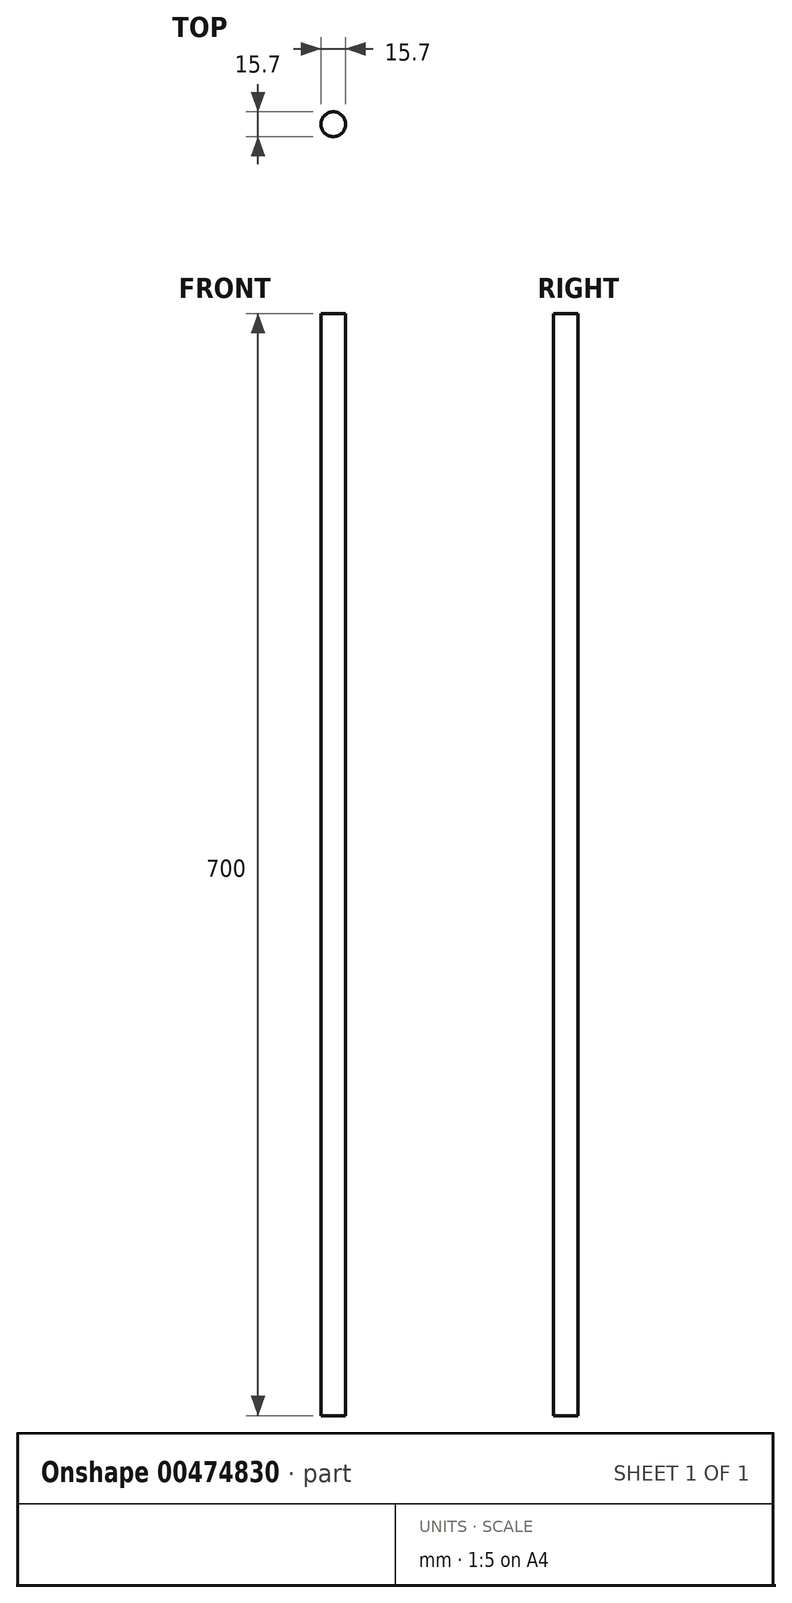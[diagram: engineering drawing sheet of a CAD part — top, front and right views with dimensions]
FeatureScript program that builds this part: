
annotation { "Feature Type Name" : "Feature", "Feature Type Description" : "" }
export const myFeature = defineFeature(function(context is Context, id is Id, definition is map)
    precondition{}
    {
        {
            var Q0;
            Q0=qCreatedBy(makeId("Top.planeOp"), FACE);
            var sketch = newSketch(context, id + "F0", { "sketchPlane" : qUnion([Q0])});
            skCircle(sketch, "E0", {"center": v(0, 0) * mm, "radius": 7.85 * mm});
            skSolve(sketch);
        }
        {
            var Q0;
            Q0 = qSketchRegion(id + "F0", true);
            extrude(context, id + "F1", {"entities" : qUnion([Q0]), "depth" : 700 * mm, "offsetDistance" : 25 * mm});
        }
    });
